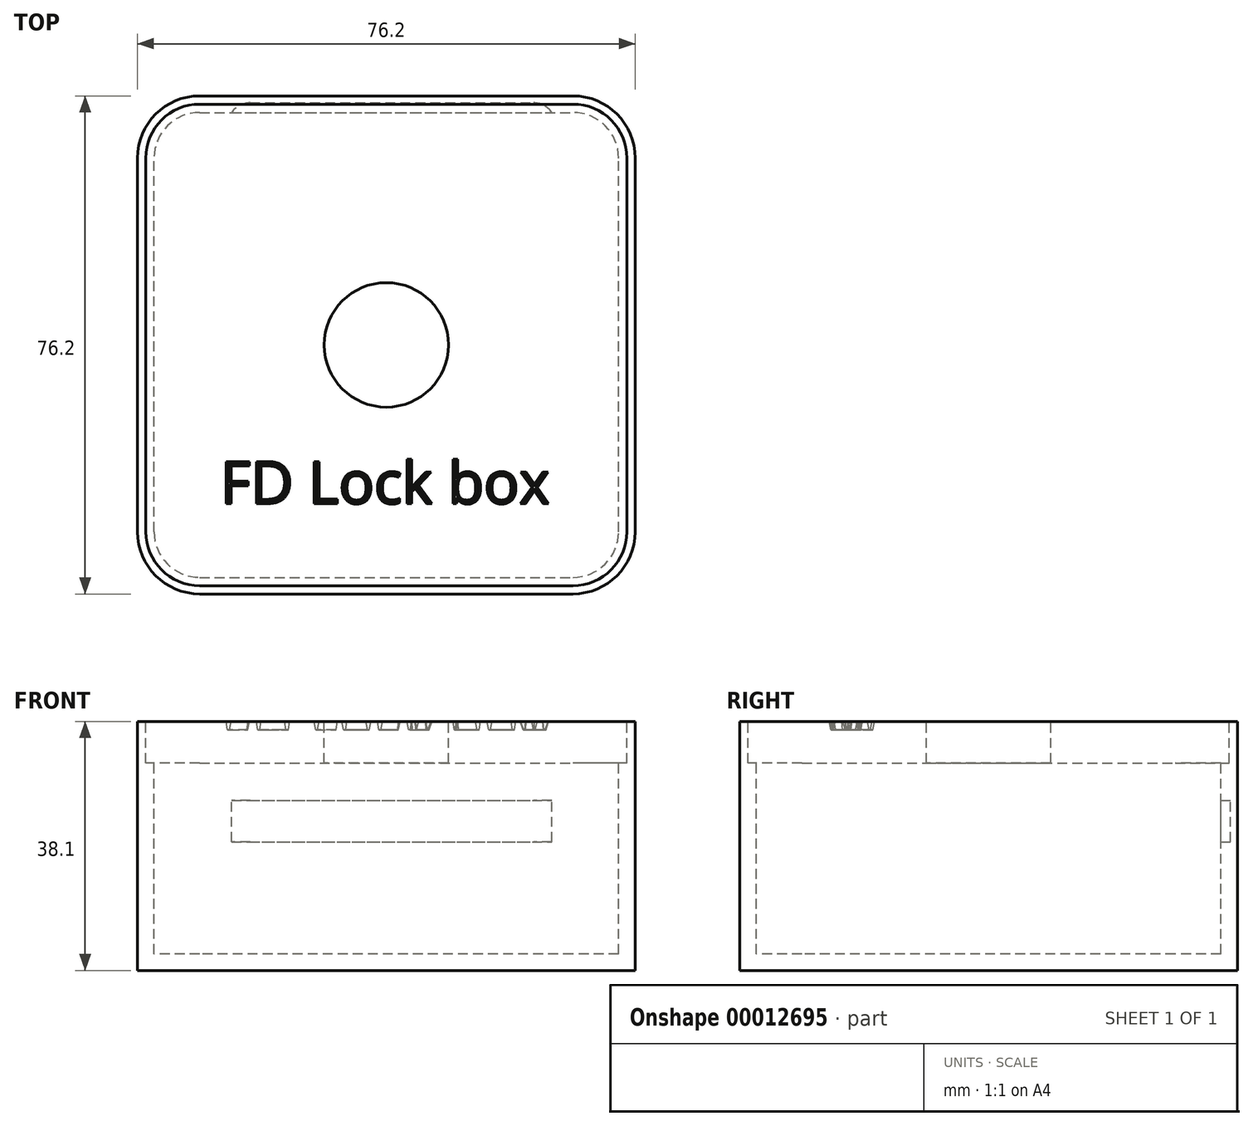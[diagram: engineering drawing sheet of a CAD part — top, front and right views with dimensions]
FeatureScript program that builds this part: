
annotation { "Feature Type Name" : "Feature", "Feature Type Description" : "" }
export const myFeature = defineFeature(function(context is Context, id is Id, definition is map)
    precondition{}
    {
        {
            var Q0;
            Q0=qCreatedBy(makeId("Top.planeOp"),FACE);
            var sketch = newSketch(context, id + "F0", { "sketchPlane" : qUnion([Q0])});
            skLineSegment(sketch, "E0.bottom", {"start": v(38.1, 38.1) * mm, "end": v(-38.1, 38.1) * mm});
            skLineSegment(sketch, "E0.top", {"start": v(38.1, -38.1) * mm, "end": v(-38.1, -38.1) * mm});
            skLineSegment(sketch, "E0.left", {"start": v(38.1, 38.1) * mm, "end": v(38.1, -38.1) * mm});
            skLineSegment(sketch, "E0.right", {"start": v(-38.1, 38.1) * mm, "end": v(-38.1, -38.1) * mm});
            skPoint(sketch, "E0.middle", {"position": v(0, 0) * mm});
            skSolve(sketch);
        }
        {
            var Q0;
            Q0=makeQuery(id+"F0.imprint","IMPRINT",FACE,{"disambiguationData":[TD([[makeQuery(id+"F0.imprint","IMPRINT",EDGE,{"derivedFrom":sQuery(id+"F0.wireOp",EDGE,"E0.bottom")}),1.0]])]});
            extrude(context, id + "F1", {"entities" : qUnion([Q0]), "oppositeDirection" : true, "depth" : 38.1 * mm, "offsetDistance" : 25.4 * mm});
        }
        {
            var Q0;
            Q0=makeQuery(id+"F1.opExtrude","SWEPT_EDGE",EDGE,{"disambiguationData":[OSD([sQuery(id+"F0.wireOp",EDGE,"36996022-4109-46c6-9681-145416d48a3c.rect.top"),sQuery(id+"F0.wireOp",EDGE,"36996022-4109-46c6-9681-145416d48a3c.rect.right")])]});
            var Q1;
            Q1=makeQuery(id+"F1.opExtrude","SWEPT_EDGE",EDGE,{"disambiguationData":[OSD([sQuery(id+"F0.wireOp",EDGE,"36996022-4109-46c6-9681-145416d48a3c.rect.top"),sQuery(id+"F0.wireOp",EDGE,"36996022-4109-46c6-9681-145416d48a3c.rect.left")])]});
            var Q2;
            Q2=makeQuery(id+"F1.opExtrude","SWEPT_EDGE",EDGE,{"disambiguationData":[OSD([sQuery(id+"F0.wireOp",EDGE,"36996022-4109-46c6-9681-145416d48a3c.rect.bottom"),sQuery(id+"F0.wireOp",EDGE,"36996022-4109-46c6-9681-145416d48a3c.rect.left")])]});
            var Q3;
            Q3=makeQuery(id+"F1.opExtrude","SWEPT_EDGE",EDGE,{"disambiguationData":[OSD([sQuery(id+"F0.wireOp",EDGE,"36996022-4109-46c6-9681-145416d48a3c.rect.bottom"),sQuery(id+"F0.wireOp",EDGE,"36996022-4109-46c6-9681-145416d48a3c.rect.right")])]});
            var Q4;
            Q4=makeQuery(id+"F1.opExtrude","SWEPT_EDGE",EDGE,{"disambiguationData":[OSD([sQuery(id+"F0.wireOp",EDGE,"E0.top"),sQuery(id+"F0.wireOp",EDGE,"E0.left")])]});
            var Q5;
            Q5=makeQuery(id+"F1.opExtrude","SWEPT_EDGE",EDGE,{"disambiguationData":[OSD([sQuery(id+"F0.wireOp",EDGE,"E0.top"),sQuery(id+"F0.wireOp",EDGE,"E0.right")])]});
            var Q6;
            Q6=makeQuery(id+"F1.opExtrude","SWEPT_EDGE",EDGE,{"disambiguationData":[OSD([sQuery(id+"F0.wireOp",EDGE,"E0.bottom"),sQuery(id+"F0.wireOp",EDGE,"E0.left")])]});
            var Q7;
            Q7=makeQuery(id+"F1.opExtrude","SWEPT_EDGE",EDGE,{"disambiguationData":[OSD([sQuery(id+"F0.wireOp",EDGE,"E0.bottom"),sQuery(id+"F0.wireOp",EDGE,"E0.right")])]});
            fillet(context, id + "F2", {"entities" : qUnion([Q0, Q1, Q2, Q3, Q4, Q5, Q6, Q7]), "radius" : 9.52 * mm, "tangentPropagation" : true, "allowEdgeOverflow" : false});
        }
        {
            var Q0;
            Q0=makeQuery(id+"F1.opExtrude","CAP_FACE",FACE,{"disambiguationData":[OSD([sQuery(id+"F0.wireOp",EDGE,"36996022-4109-46c6-9681-145416d48a3c.rect.bottom"),sQuery(id+"F0.wireOp",EDGE,"36996022-4109-46c6-9681-145416d48a3c.rect.top"),sQuery(id+"F0.wireOp",EDGE,"36996022-4109-46c6-9681-145416d48a3c.rect.left"),sQuery(id+"F0.wireOp",EDGE,"36996022-4109-46c6-9681-145416d48a3c.rect.right")])],"isStart":true});
            var Q1;
            Q1=makeQuery(id+"F1.opExtrude","CAP_FACE",FACE,{"disambiguationData":[OSD([sQuery(id+"F0.wireOp",EDGE,"E0.bottom"),sQuery(id+"F0.wireOp",EDGE,"E0.top"),sQuery(id+"F0.wireOp",EDGE,"E0.left"),sQuery(id+"F0.wireOp",EDGE,"E0.right")])],"isStart":true});
            shell(context, id + "F3", {"entities" : qUnion([Q0, Q1]), "thickness" : 2.54 * mm});
        }
        {
            var Q0;
            Q0=makeQuery(id+"F1.opExtrude","CAP_FACE",FACE,{"disambiguationData":[OSD([sQuery(id+"F0.wireOp",EDGE,"36996022-4109-46c6-9681-145416d48a3c.rect.bottom"),sQuery(id+"F0.wireOp",EDGE,"36996022-4109-46c6-9681-145416d48a3c.rect.top"),sQuery(id+"F0.wireOp",EDGE,"36996022-4109-46c6-9681-145416d48a3c.rect.left"),sQuery(id+"F0.wireOp",EDGE,"36996022-4109-46c6-9681-145416d48a3c.rect.right")])],"isStart":true});
            var Q1;
            Q1=makeQuery(id+"F0.imprint","IMPRINT",FACE,{"disambiguationData":[TD([[makeQuery(id+"F0.imprint","IMPRINT",EDGE,{"derivedFrom":sQuery(id+"F0.wireOp",EDGE,"E0.bottom")}),1.0]])]});
            cPlane(context, id + "F4", {"entities" : qUnion([Q0, Q1]), "cplaneType" : CPlaneType.OFFSET, "offset" : 15.24 * mm, "oppositeDirection" : true, "width" : 152.4 * mm, "height" : 152.4 * mm});
        }
        {
            var Q0;
            Q0=qCreatedBy(id+"F4.planeOp",FACE);
            var sketch = newSketch(context, id + "F5", { "sketchPlane" : qUnion([Q0])});
            skLineSegment(sketch, "E1", {"start": v(-20.86, 37.04) * mm, "end": v(22.52, 37.04) * mm});
            skLineSegment(sketch, "E2", {"start": v(25.94, 33.61) * mm, "end": v(25.94, 30.85) * mm});
            skLineSegment(sketch, "E3", {"start": v(25.94, 30.85) * mm, "end": v(-24.29, 31.44) * mm});
            skLineSegment(sketch, "E4", {"start": v(-24.29, 31.44) * mm, "end": v(-24.29, 33.61) * mm});
            skPoint(sketch, "E5.visualSharp", {"position": v(-24.29, 37.04) * mm});
            skArc(sketch, "E5.filletArc", {"start": v(-20.86, 37.04) * mm, "mid": v(-23.28, 36.04) * mm, "end": v(-24.29, 33.61) * mm});
            skPoint(sketch, "E6.visualSharp", {"position": v(25.94, 37.04) * mm});
            skArc(sketch, "E6.filletArc", {"start": v(25.94, 33.61) * mm, "mid": v(24.94, 36.04) * mm, "end": v(22.52, 37.04) * mm});
            skSolve(sketch);
        }
        {
            var Q0;
            Q0=qSketchRegion(id+"F5",true);
            extrude(context, id + "F6", {"entities" : qUnion([Q0]), "operationType" : NewBodyOperationType.REMOVE, "endBound" : BoundingType.SYMMETRIC, "oppositeDirection" : true, "depth" : 6.35 * mm});
        }
        {
            var Q0;
            Q0=makeQuery(id+"F0.imprint","IMPRINT",FACE,{"disambiguationData":[TD([[makeQuery(id+"F0.imprint","IMPRINT",EDGE,{"derivedFrom":sQuery(id+"F0.wireOp",EDGE,"E0.bottom")}),1.0]])]});
            cPlane(context, id + "F7", {"entities" : qUnion([Q0]), "cplaneType" : CPlaneType.OFFSET, "offset" : 0 * mm, "width" : 152.4 * mm, "height" : 152.4 * mm});
        }
        {
            var Q0;
            Q0=qCreatedBy(id+"F7.planeOp",FACE);
            var sketch = newSketch(context, id + "F8", { "sketchPlane" : qUnion([Q0])});
            skLineSegment(sketch, "E7.0", {"start": v(28.57, 36.83) * mm, "end": v(-28.58, 36.83) * mm});
            skArc(sketch, "E7.1", {"start": v(36.83, 28.58) * mm, "mid": v(34.41, 34.41) * mm, "end": v(28.57, 36.83) * mm});
            skArc(sketch, "E7.2", {"start": v(-28.58, 36.83) * mm, "mid": v(-34.41, 34.41) * mm, "end": v(-36.83, 28.58) * mm});
            skLineSegment(sketch, "E7.3", {"start": v(36.83, 28.58) * mm, "end": v(36.83, -28.58) * mm});
            skLineSegment(sketch, "E7.4", {"start": v(-36.83, 28.58) * mm, "end": v(-36.83, -28.58) * mm});
            skArc(sketch, "E7.5", {"start": v(-36.83, -28.58) * mm, "mid": v(-34.41, -34.41) * mm, "end": v(-28.57, -36.83) * mm});
            skLineSegment(sketch, "E7.6", {"start": v(28.58, -36.83) * mm, "end": v(-28.57, -36.83) * mm});
            skArc(sketch, "E7.7", {"start": v(28.58, -36.83) * mm, "mid": v(34.41, -34.41) * mm, "end": v(36.83, -28.58) * mm});
            skSolve(sketch);
        }
        {
            var Q0;
            Q0 = qSketchRegion(id + "F8", true);
            extrude(context, id + "F9", {"entities" : qUnion([Q0]), "operationType" : NewBodyOperationType.REMOVE, "oppositeDirection" : true, "depth" : 6.35 * mm, "offsetDistance" : 25.4 * mm});
        }
        {
            var Q0;
            Q0=makeQuery(id+"F9.boolean.opBoolean","INTERSECT",EDGE,{"derivedFrom":[makeQuery(id+"F3.opShell","OFFSET_FACE",FACE,{"disambiguationData":[OSD([sQuery(id+"F0.wireOp",EDGE,"E0.right")])]}),makeQuery(id+"F9.opExtrude","CAP_FACE",FACE,{"disambiguationData":[OSD([sQuery(id+"F8.wireOp",EDGE,"E7.0"),sQuery(id+"F8.wireOp",EDGE,"E7.1"),sQuery(id+"F8.wireOp",EDGE,"E7.2"),sQuery(id+"F8.wireOp",EDGE,"E7.3"),sQuery(id+"F8.wireOp",EDGE,"E7.4"),sQuery(id+"F8.wireOp",EDGE,"E7.5"),sQuery(id+"F8.wireOp",EDGE,"E7.6"),sQuery(id+"F8.wireOp",EDGE,"E7.7")])],"isStart":false})]});
            cPlane(context, id + "F10", {"entities" : qUnion([Q0]), "cplaneType" : CPlaneType.LINE_ANGLE, "offset" : 25.4 * mm, "angle" : 0 * degree, "width" : 152.4 * mm, "height" : 152.4 * mm});
        }
        {
            var Q0;
            Q0=qCreatedBy(id+"F10.planeOp",FACE);
            var sketch = newSketch(context, id + "F11", { "sketchPlane" : qUnion([Q0])});
            skLineSegment(sketch, "E8.0", {"start": v(28.57, 36.83) * mm, "end": v(-28.58, 36.83) * mm});
            skArc(sketch, "E8.1", {"start": v(-28.58, 36.83) * mm, "mid": v(-34.41, 34.41) * mm, "end": v(-36.83, 28.58) * mm});
            skLineSegment(sketch, "E8.2", {"start": v(-36.83, 28.58) * mm, "end": v(-36.83, -28.58) * mm});
            skArc(sketch, "E8.3", {"start": v(-36.83, -28.58) * mm, "mid": v(-34.41, -34.41) * mm, "end": v(-28.57, -36.83) * mm});
            skLineSegment(sketch, "E8.4", {"start": v(28.58, -36.83) * mm, "end": v(-28.57, -36.83) * mm});
            skArc(sketch, "E8.5", {"start": v(28.58, -36.83) * mm, "mid": v(34.41, -34.41) * mm, "end": v(36.83, -28.58) * mm});
            skLineSegment(sketch, "E8.6", {"start": v(36.83, 28.58) * mm, "end": v(36.83, -28.58) * mm});
            skArc(sketch, "E8.7", {"start": v(36.83, 28.58) * mm, "mid": v(34.41, 34.41) * mm, "end": v(28.57, 36.83) * mm});
            skSolve(sketch);
        }
        {
            var Q0;
            Q0 = qSketchRegion(id + "F11", true);
            extrude(context, id + "F12", {"entities" : qUnion([Q0]), "depth" : 6.35 * mm, "offsetDistance" : 25.4 * mm});
        }
        {
            var Q0;
            Q0=makeQuery(id+"F0.imprint","IMPRINT",FACE,{"disambiguationData":[TD([[makeQuery(id+"F0.imprint","IMPRINT",EDGE,{"derivedFrom":sQuery(id+"F0.wireOp",EDGE,"E0.bottom")}),1.0]])]});
            var sketch = newSketch(context, id + "F13", { "sketchPlane" : qUnion([Q0])});
            skCircle(sketch, "E9", {"center": v(0, 0) * mm, "radius": 9.53 * mm});
            skSolve(sketch);
        }
        {
            var Q0;
            Q0 = qSketchRegion(id + "F13", true);
            extrude(context, id + "F14", {"entities" : qUnion([Q0]), "operationType" : NewBodyOperationType.REMOVE, "endBound" : BoundingType.UP_TO_NEXT, "oppositeDirection" : true, "depth" : 25.4 * mm, "offsetDistance" : 25.4 * mm});
        }
        {
            var Q0;
            Q0=makeQuery(id+"F12.opExtrude","CAP_FACE",FACE,{"disambiguationData":[OSD([sQuery(id+"F11.wireOp",EDGE,"E8.0"),sQuery(id+"F11.wireOp",EDGE,"E8.1"),sQuery(id+"F11.wireOp",EDGE,"E8.2"),sQuery(id+"F11.wireOp",EDGE,"E8.3"),sQuery(id+"F11.wireOp",EDGE,"E8.4"),sQuery(id+"F11.wireOp",EDGE,"E8.5"),sQuery(id+"F11.wireOp",EDGE,"E8.6"),sQuery(id+"F11.wireOp",EDGE,"E8.7")])],"isStart":false});
            var sketch = newSketch(context, id + "F15", { "sketchPlane" : qUnion([Q0])});
            skText(sketch, "E10", { "text": "FD Lock box", "fontName": "OpenSans-Regular.ttf"});
            const initialGuessF15  = {"E10": [-0.0254, -0.02427, 1, 0, 0.00645]};
            skSetInitialGuess(sketch, initialGuessF15);
            skSolve(sketch);
        }
        {
            var Q0;
            Q0 = qSketchRegion(id + "F15", true);
            extrude(context, id + "F16", {"entities" : qUnion([Q0]), "operationType" : NewBodyOperationType.REMOVE, "oppositeDirection" : true, "depth" : 1.27 * mm, "offsetDistance" : 25.4 * mm, "hasDraft" : true, "draftAngle" : 10 * degree, "draftPullDirection" : true});
        }
    });
